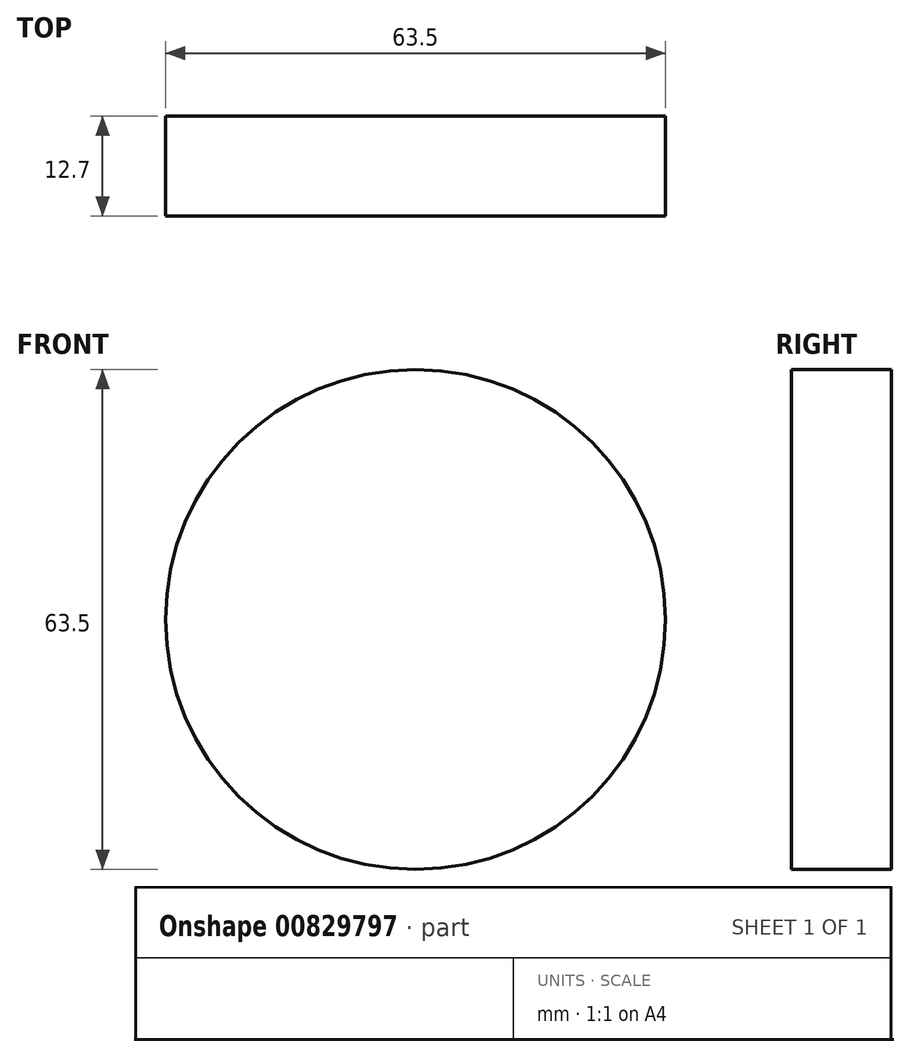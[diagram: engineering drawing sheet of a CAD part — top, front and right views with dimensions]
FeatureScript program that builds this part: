
annotation { "Feature Type Name" : "Feature", "Feature Type Description" : "" }
export const myFeature = defineFeature(function(context is Context, id is Id, definition is map)
    precondition{}
    {
        {
            var Q0;
            Q0=qCreatedBy(makeId("Front.planeOp"),FACE);
            var sketch = newSketch(context, id + "F0", { "sketchPlane" : qUnion([Q0])});
            skCircle(sketch, "E0", {"center": v(0, 0) * mm, "radius": 31.75 * mm});
            skSolve(sketch);
        }
        {
            var Q0;
            Q0=makeQuery(id+"F0.imprint","IMPRINT",FACE,{"disambiguationData":[TD([[makeQuery(id+"F0.imprint","IMPRINT",EDGE,{"derivedFrom":sQuery(id+"F0.wireOp",EDGE,"E0")}),1.0]])]});
            extrude(context, id + "F1", {"entities" : qUnion([Q0]), "depth" : 12.7 * mm, "offsetDistance" : 25.4 * mm});
        }
    });
